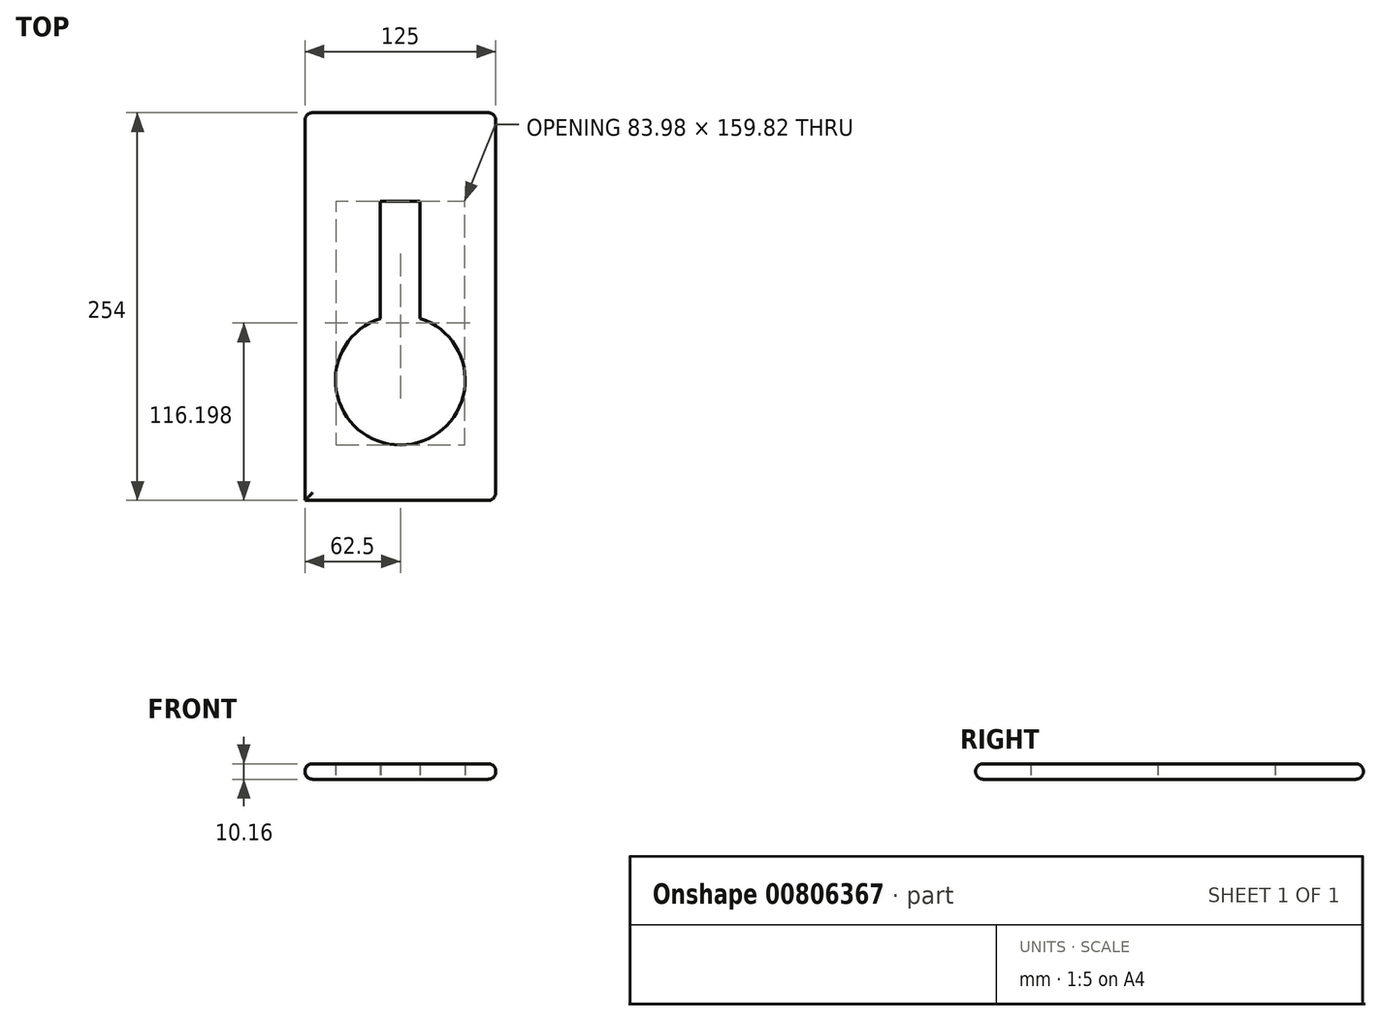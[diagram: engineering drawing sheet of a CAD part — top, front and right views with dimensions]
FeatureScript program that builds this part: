
annotation { "Feature Type Name" : "Feature", "Feature Type Description" : "" }
export const myFeature = defineFeature(function(context is Context, id is Id, definition is map)
    precondition{}
    {
        {
            var Q0;
            Q0=qCreatedBy(makeId("Top.planeOp"),FACE);
            var sketch = newSketch(context, id + "F0", { "sketchPlane" : qUnion([Q0])});
            skLineSegment(sketch, "E0.bottom", {"start": v(-62.5, 134.75) * mm, "end": v(62.5, 134.75) * mm});
            skLineSegment(sketch, "E0.top", {"start": v(-62.5, -119.25) * mm, "end": v(62.5, -119.25) * mm});
            skLineSegment(sketch, "E0.left", {"start": v(-62.5, 134.75) * mm, "end": v(-62.5, -119.25) * mm});
            skLineSegment(sketch, "E0.right", {"start": v(62.5, 134.75) * mm, "end": v(62.5, -119.25) * mm});
            skCircle(sketch, "E1", {"center": v(0, -40.46) * mm, "radius": 42.5 * mm});
            skLineSegment(sketch, "E2", {"start": v(13, 0) * mm, "end": v(13, 76.86) * mm});
            skLineSegment(sketch, "E3", {"start": v(13, 76.86) * mm, "end": v(-13.05, 76.86) * mm});
            skLineSegment(sketch, "E4", {"start": v(-13.05, 76.86) * mm, "end": v(-13.05, 0) * mm});
            skLineSegment(sketch, "E5", {"start": v(-13.05, 0) * mm, "end": v(13, 0) * mm});
            skSolve(sketch);
        }
        {
            var Q0;
            Q0=makeQuery(id+"F0.imprint","IMPRINT",FACE,{"disambiguationData":[TD([[makeQuery(id+"F0.imprint","IMPRINT",EDGE,{"derivedFrom":sQuery(id+"F0.wireOp",EDGE,"E0.bottom")}),-1.0]])]});
            extrude(context, id + "F1", {"entities" : qUnion([Q0]), "depth" : 10.16 * mm, "offsetDistance" : 25.4 * mm});
        }
        {
            var Q0;
            Q0=makeQuery(id+"F1.opExtrude","CAP_EDGE",EDGE,{"disambiguationData":[OSD([sQuery(id+"F0.wireOp",EDGE,"E0.bottom")])],"isStart":false});
            var Q1;
            Q1=makeQuery(id+"F1.opExtrude","SWEPT_EDGE",EDGE,{"disambiguationData":[OSD([sQuery(id+"F0.wireOp",EDGE,"E0.bottom"),sQuery(id+"F0.wireOp",EDGE,"E0.left")])]});
            var Q2;
            Q2=makeQuery(id+"F1.opExtrude","CAP_EDGE",EDGE,{"disambiguationData":[OSD([sQuery(id+"F0.wireOp",EDGE,"E0.left")])],"isStart":false});
            var Q3;
            Q3=makeQuery(id+"F1.opExtrude","CAP_EDGE",EDGE,{"disambiguationData":[OSD([sQuery(id+"F0.wireOp",EDGE,"E0.right")])],"isStart":false});
            var Q4;
            Q4=makeQuery(id+"F1.opExtrude","CAP_EDGE",EDGE,{"disambiguationData":[OSD([sQuery(id+"F0.wireOp",EDGE,"E0.top")])],"isStart":false});
            var Q5;
            Q5=makeQuery(id+"F1.opExtrude","CAP_EDGE",EDGE,{"disambiguationData":[OSD([sQuery(id+"F0.wireOp",EDGE,"E0.left")])],"isStart":true});
            var Q6;
            Q6=makeQuery(id+"F1.opExtrude","SWEPT_FACE",FACE,{"disambiguationData":[OSD([sQuery(id+"F0.wireOp",EDGE,"E0.right")])]});
            var Q7;
            Q7=makeQuery(id+"F1.opExtrude","CAP_EDGE",EDGE,{"disambiguationData":[OSD([sQuery(id+"F0.wireOp",EDGE,"E0.top")])],"isStart":true});
            var Q8;
            Q8=makeQuery(id+"F1.opExtrude","CAP_EDGE",EDGE,{"disambiguationData":[OSD([sQuery(id+"F0.wireOp",EDGE,"E0.bottom")])],"isStart":true});
            fillet(context, id + "F2", {"entities" : qUnion([Q0, Q1, Q2, Q3, Q4, Q5, Q6, Q7, Q8]), "radius" : 5.08 * mm, "tangentPropagation" : true, "allowEdgeOverflow" : false});
        }
    });
